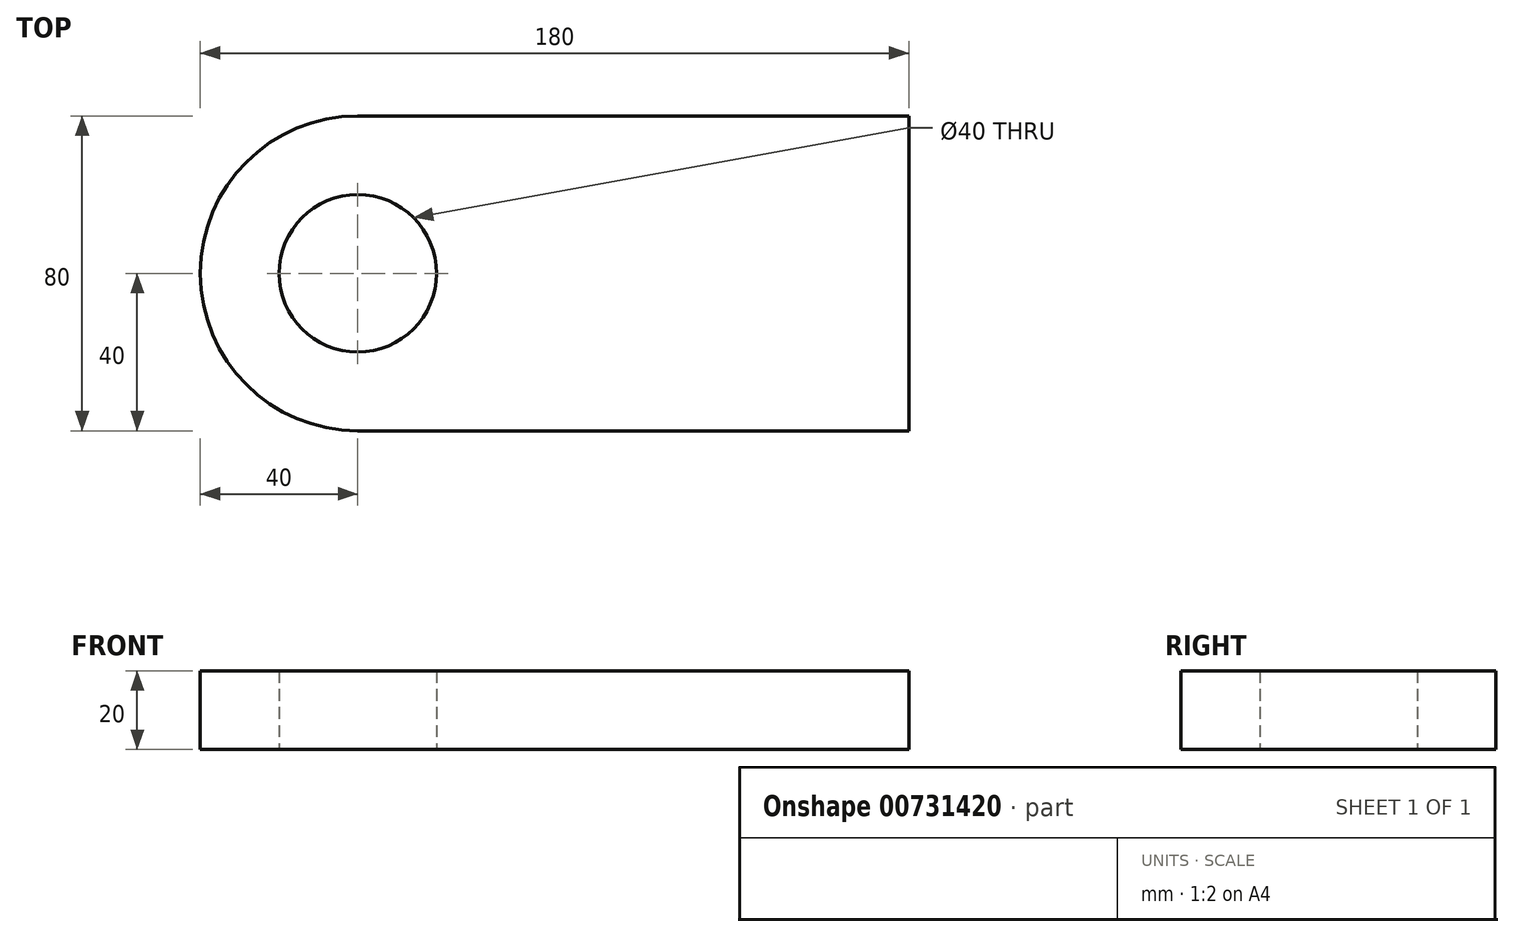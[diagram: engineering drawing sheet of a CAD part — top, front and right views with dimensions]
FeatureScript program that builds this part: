
annotation { "Feature Type Name" : "Feature", "Feature Type Description" : "" }
export const myFeature = defineFeature(function(context is Context, id is Id, definition is map)
    precondition{}
    {
        {
            var Q0;
            Q0=qCreatedBy(makeId("Top.planeOp"),FACE);
            var sketch = newSketch(context, id + "F0", { "sketchPlane" : qUnion([Q0])});
            skLineSegment(sketch, "E0.bottom", {"start": v(70, 40) * mm, "end": v(-70, 40) * mm});
            skLineSegment(sketch, "E0.top", {"start": v(70, -40) * mm, "end": v(-70, -40) * mm});
            skLineSegment(sketch, "E0.left", {"start": v(70, 40) * mm, "end": v(70, -40) * mm});
            skLineSegment(sketch, "E0.right", {"start": v(-70, 40) * mm, "end": v(-70, -40) * mm});
            skPoint(sketch, "E0.middle", {"position": v(0, 0) * mm});
            skLineSegment(sketch, "E1", {"start": v(70, 40) * mm, "end": v(14, 40) * mm});
            skLineSegment(sketch, "E2", {"start": v(14, 40) * mm, "end": v(14, -40) * mm});
            skLineSegment(sketch, "E3", {"start": v(14, -40) * mm, "end": v(-26, -40) * mm});
            skLineSegment(sketch, "E4", {"start": v(70, -40) * mm, "end": v(70, -20) * mm});
            skLineSegment(sketch, "E5", {"start": v(70, -20) * mm, "end": v(70, 20) * mm});
            skCircle(sketch, "E6", {"center": v(-70, 0) * mm, "radius": 20 * mm});
            skCircle(sketch, "E7", {"center": v(-70, 0) * mm, "radius": 40 * mm});
            skLineSegment(sketch, "E8", {"start": v(14, 40) * mm, "end": v(0, 40) * mm});
            skLineSegment(sketch, "E9", {"start": v(14, 40) * mm, "end": v(-30, 40) * mm});
            skLineSegment(sketch, "E10", {"start": v(-30, 40) * mm, "end": v(-30, -40) * mm});
            skLineSegment(sketch, "E11", {"start": v(-30, -40) * mm, "end": v(14, -40) * mm});
            skSolve(sketch);
        }
        {
            var Q0;
            Q0 = qSketchRegion(id + "F0", true);
            extrude(context, id + "F1", {"entities" : qUnion([Q0]), "depth" : 20 * mm, "offsetDistance" : 25 * mm});
        }
    });
